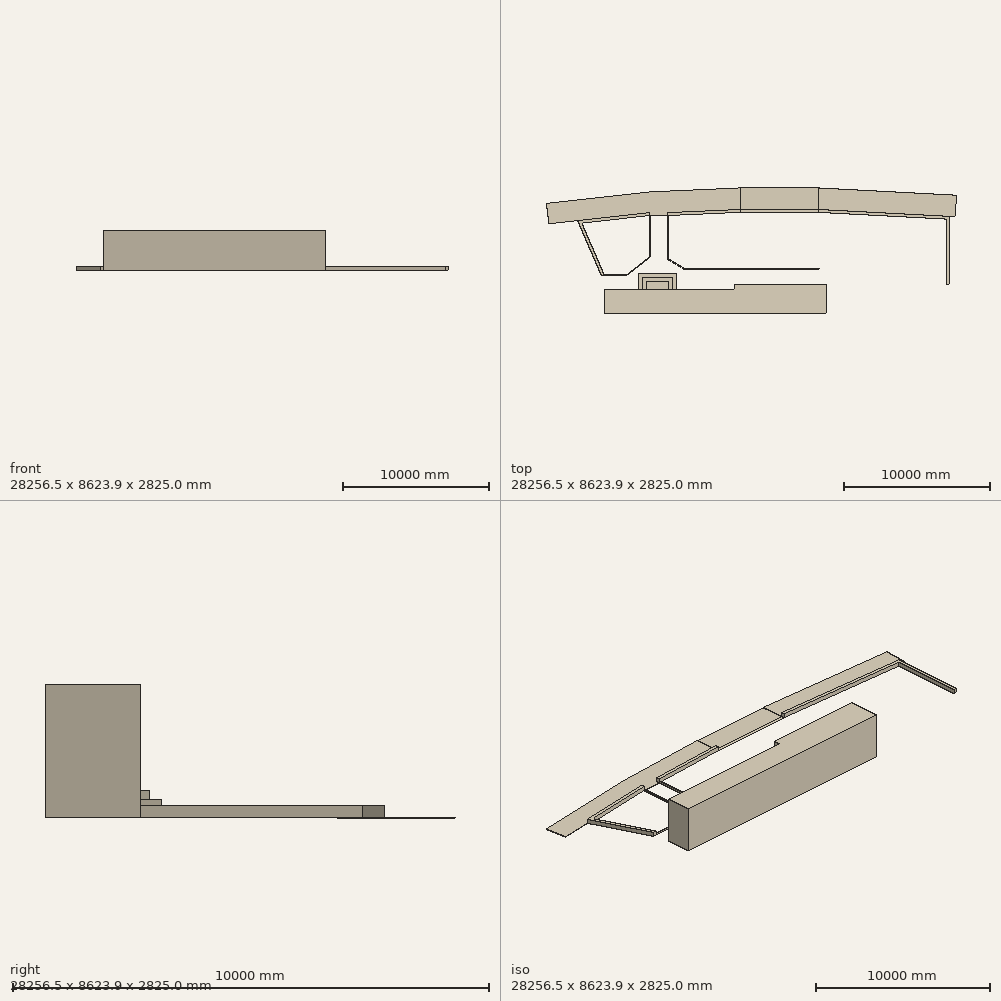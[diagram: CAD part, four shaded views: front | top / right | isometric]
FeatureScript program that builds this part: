
annotation { "Feature Type Name" : "Feature", "Feature Type Description" : "" }
export const myFeature = defineFeature(function(context is Context, id is Id, definition is map)
    precondition{}
    {
        {
            var Q0;
            Q0=qCreatedBy(makeId("Top.planeOp"),FACE);
            var sketch = newSketch(context, id + "F0", { "sketchPlane" : qUnion([Q0])});
            skLineSegment(sketch, "E0", {"start": v(0, 1000) * mm, "end": v(1590, 1000) * mm});
            skLineSegment(sketch, "E1", {"start": v(0, 1000) * mm, "end": v(-1557.02, 4597.51) * mm});
            skLineSegment(sketch, "E2", {"start": v(-1557.02, 4597.51) * mm, "end": v(3143.94, 5120.86) * mm});
            skLineSegment(sketch, "E3", {"start": v(3143.94, 5120.86) * mm, "end": v(3143.94, 2210.86) * mm});
            skLineSegment(sketch, "E4", {"start": v(3143.94, 2210.86) * mm, "end": v(1590, 1000) * mm});
            skLineSegment(sketch, "E5", {"start": v(4373.94, 5120.86) * mm, "end": v(9373.94, 5340) * mm});
            skLineSegment(sketch, "E6", {"start": v(9373.94, 5340) * mm, "end": v(14723.94, 5340) * mm, "construction": true});
            skLineSegment(sketch, "E7", {"start": v(14723.94, 5340) * mm, "end": v(23582.98, 4875.72) * mm});
            skLineSegment(sketch, "E8", {"start": v(23582.98, 4875.72) * mm, "end": v(23582.98, 400) * mm});
            skLineSegment(sketch, "E9", {"start": v(4373.94, 5120.86) * mm, "end": v(4373.94, 2100.86) * mm});
            skLineSegment(sketch, "E10", {"start": v(4373.94, 2100.86) * mm, "end": v(5527.75, 1400) * mm});
            skLineSegment(sketch, "E11", {"start": v(5527.75, 1400) * mm, "end": v(14847.75, 1400) * mm});
            skLineSegment(sketch, "E12", {"start": v(14847.75, 1400) * mm, "end": v(14847.75, 400) * mm});
            skLineSegment(sketch, "E13", {"start": v(0, 0) * mm, "end": v(8970, 0) * mm});
            skLineSegment(sketch, "E14", {"start": v(8970, 0) * mm, "end": v(8970, 400) * mm});
            skLineSegment(sketch, "E15", {"start": v(8970, 400) * mm, "end": v(14847.75, 400) * mm});
            skLineSegment(sketch, "E16", {"start": v(0, 0) * mm, "end": v(0, 1000) * mm, "construction": true});
            skLineSegment(sketch, "E17", {"start": v(3143.94, 5120.86) * mm, "end": v(4373.94, 5120.86) * mm, "construction": true});
            skLineSegment(sketch, "E18", {"start": v(2360, 0) * mm, "end": v(2360, 1120) * mm});
            skLineSegment(sketch, "E19", {"start": v(2360, 1120) * mm, "end": v(4990, 1120) * mm});
            skLineSegment(sketch, "E20", {"start": v(4990, 1120) * mm, "end": v(4990, 0) * mm});
            skLineSegment(sketch, "E21", {"start": v(2642.5, 0) * mm, "end": v(2642.5, 850) * mm});
            skLineSegment(sketch, "E22", {"start": v(2642.5, 850) * mm, "end": v(4707.5, 850) * mm});
            skLineSegment(sketch, "E23", {"start": v(4707.5, 850) * mm, "end": v(4707.5, 0) * mm});
            skLineSegment(sketch, "E24", {"start": v(2925, 0) * mm, "end": v(2925, 580) * mm});
            skLineSegment(sketch, "E25", {"start": v(2925, 580) * mm, "end": v(4425, 580) * mm});
            skLineSegment(sketch, "E26", {"start": v(4425, 580) * mm, "end": v(4425, 0) * mm});
            skLineSegment(sketch, "E27", {"start": v(2360, 1120) * mm, "end": v(2642.5, 850) * mm, "construction": true});
            skLineSegment(sketch, "E28", {"start": v(2642.5, 850) * mm, "end": v(2925, 580) * mm, "construction": true});
            skLineSegment(sketch, "E29", {"start": v(4425, 580) * mm, "end": v(4707.5, 850) * mm, "construction": true});
            skLineSegment(sketch, "E30", {"start": v(4707.5, 850) * mm, "end": v(4990, 1120) * mm, "construction": true});
            skLineSegment(sketch, "E31", {"start": v(2360, 1120) * mm, "end": v(2360, 1600) * mm, "construction": true});
            skLineSegment(sketch, "E32", {"start": v(-3990.98, 5956.54) * mm, "end": v(3143.94, 6750.86) * mm});
            skLineSegment(sketch, "E33", {"start": v(3143.94, 6750.86) * mm, "end": v(9373.94, 7023.9) * mm});
            skLineSegment(sketch, "E34", {"start": v(9373.94, 7023.9) * mm, "end": v(14723.94, 7023.9) * mm});
            skLineSegment(sketch, "E35", {"start": v(14723.94, 7023.9) * mm, "end": v(24265.47, 6523.86) * mm});
            skLineSegment(sketch, "E36", {"start": v(4373.94, 5120.86) * mm, "end": v(4373.94, 7645.58) * mm, "construction": true});
            skSolve(sketch);
        }
        {
            var Q0;
            {var subQ0=sQuery(id+"F0.wireOp",EDGE,"E24");Q0=makeQuery(id+"F0.imprint","IMPRINT",FACE,{"disambiguationData":[TD([[makeQuery(id+"F0.imprint","IMPRINT",EDGE,{"derivedFrom":subQ0}),-1.0]])]});}
            var sketch = newSketch(context, id + "F1", { "sketchPlane" : qUnion([Q0])});
            skLineSegment(sketch, "E37.bottom", {"start": v(4990, 1120) * mm, "end": v(2360, 1120) * mm});
            skLineSegment(sketch, "E37.top", {"start": v(4990, 0) * mm, "end": v(2360, 0) * mm});
            skLineSegment(sketch, "E37.left", {"start": v(4990, 1120) * mm, "end": v(4990, 0) * mm});
            skLineSegment(sketch, "E37.right", {"start": v(2360, 1120) * mm, "end": v(2360, 0) * mm});
            skSolve(sketch);
        }
        {
            var Q0;
            Q0 = qSketchRegion(id + "F1", true);
            extrude(context, id + "F2", {"entities" : qUnion([Q0]), "depth" : 190 * mm});
        }
        {
            var Q0;
            Q0=makeQuery(id+"F2.opExtrude","CAP_FACE",FACE,{"disambiguationData":[OSD([sQuery(id+"F1.wireOp",EDGE,"E37.bottom"),sQuery(id+"F1.wireOp",EDGE,"E37.top"),sQuery(id+"F1.wireOp",EDGE,"E37.left"),sQuery(id+"F1.wireOp",EDGE,"E37.right")])],"isStart":false});
            var sketch = newSketch(context, id + "F3", { "sketchPlane" : qUnion([Q0])});
            skLineSegment(sketch, "E38.bottom", {"start": v(4707.5, 850) * mm, "end": v(2642.5, 850) * mm});
            skLineSegment(sketch, "E38.top", {"start": v(4707.5, 0) * mm, "end": v(2642.5, 0) * mm});
            skLineSegment(sketch, "E38.left", {"start": v(4707.5, 850) * mm, "end": v(4707.5, 0) * mm});
            skLineSegment(sketch, "E38.right", {"start": v(2642.5, 850) * mm, "end": v(2642.5, 0) * mm});
            skSolve(sketch);
        }
        {
            var Q0;
            Q0 = qSketchRegion(id + "F3", true);
            extrude(context, id + "F4", {"entities" : qUnion([Q0]), "operationType" : NewBodyOperationType.ADD, "depth" : 190 * mm});
        }
        {
            var Q0;
            Q0=makeQuery(id+"F4.opExtrude","CAP_FACE",FACE,{"disambiguationData":[OSD([sQuery(id+"F3.wireOp",EDGE,"E38.bottom"),sQuery(id+"F3.wireOp",EDGE,"E38.top"),sQuery(id+"F3.wireOp",EDGE,"E38.left"),sQuery(id+"F3.wireOp",EDGE,"E38.right")])],"isStart":false});
            var sketch = newSketch(context, id + "F5", { "sketchPlane" : qUnion([Q0])});
            skLineSegment(sketch, "E39.bottom", {"start": v(4425, 580) * mm, "end": v(2925, 580) * mm});
            skLineSegment(sketch, "E39.top", {"start": v(4425, 0) * mm, "end": v(2925, 0) * mm});
            skLineSegment(sketch, "E39.left", {"start": v(4425, 580) * mm, "end": v(4425, 0) * mm});
            skLineSegment(sketch, "E39.right", {"start": v(2925, 580) * mm, "end": v(2925, 0) * mm});
            skSolve(sketch);
        }
        {
            var Q0;
            Q0 = qSketchRegion(id + "F5", true);
            extrude(context, id + "F6", {"entities" : qUnion([Q0]), "operationType" : NewBodyOperationType.ADD, "depth" : 190 * mm});
        }
        {
            var Q0;
            Q0=makeQuery(id+"F0.imprint","IMPRINT",FACE,{"disambiguationData":[TD([[makeQuery(id+"F0.imprint","IMPRINT",EDGE,{"derivedFrom":sQuery(id+"F0.wireOp",EDGE,"E0")}),1.0]])]});
            var sketch = newSketch(context, id + "F7", { "sketchPlane" : qUnion([Q0])});
            skLineSegment(sketch, "E40", {"start": v(0, 1000) * mm, "end": v(-1557.02, 4597.51) * mm});
            skLineSegment(sketch, "E41", {"start": v(-1557.02, 4597.51) * mm, "end": v(3143.94, 5120.86) * mm});
            skLineSegment(sketch, "E42", {"start": v(3143.94, 5120.86) * mm, "end": v(3121.8, 5319.63) * mm});
            skLineSegment(sketch, "E43", {"start": v(3121.8, 5319.63) * mm, "end": v(-1848.02, 4766.35) * mm});
            skLineSegment(sketch, "E44", {"start": v(-1848.02, 4766.35) * mm, "end": v(-217.93, 1000) * mm});
            skLineSegment(sketch, "E45", {"start": v(-217.93, 1000) * mm, "end": v(0, 1000) * mm});
            skLineSegment(sketch, "E46", {"start": v(-1557.02, 4597.51) * mm, "end": v(-1740.57, 4518.07) * mm, "construction": true});
            skLineSegment(sketch, "E47", {"start": v(4373.94, 5120.86) * mm, "end": v(4351.8, 5319.63) * mm});
            skLineSegment(sketch, "E48", {"start": v(4351.8, 5319.63) * mm, "end": v(9373.94, 5539.74) * mm});
            skLineSegment(sketch, "E49", {"start": v(9373.94, 5539.74) * mm, "end": v(9373.94, 5340) * mm});
            skLineSegment(sketch, "E50", {"start": v(9373.94, 5340) * mm, "end": v(4373.94, 5120.86) * mm});
            skLineSegment(sketch, "E51", {"start": v(14723.94, 5340) * mm, "end": v(14723.94, 5539.74) * mm});
            skLineSegment(sketch, "E52", {"start": v(14723.94, 5539.74) * mm, "end": v(23782.72, 5065) * mm});
            skLineSegment(sketch, "E53", {"start": v(23782.72, 5065) * mm, "end": v(23782.72, 400) * mm});
            skLineSegment(sketch, "E54", {"start": v(23782.72, 400) * mm, "end": v(23582.98, 400) * mm});
            skLineSegment(sketch, "E55", {"start": v(23582.98, 400) * mm, "end": v(23582.98, 4875.72) * mm});
            skLineSegment(sketch, "E56", {"start": v(23582.98, 4875.72) * mm, "end": v(14723.94, 5340) * mm});
            skSolve(sketch);
        }
        {
            var Q0;
            Q0 = qSketchRegion(id + "F7", true);
            extrude(context, id + "F8", {"entities" : qUnion([Q0]), "depth" : 260 * mm});
        }
        {
            var Q0;
            Q0=makeQuery(id+"F0.imprint","IMPRINT",FACE,{"disambiguationData":[TD([[makeQuery(id+"F0.imprint","IMPRINT",EDGE,{"derivedFrom":sQuery(id+"F0.wireOp",EDGE,"E0")}),1.0]])]});
            var sketch = newSketch(context, id + "F9", { "sketchPlane" : qUnion([Q0])});
            skLineSegment(sketch, "E57", {"start": v(4373.94, 5120.86) * mm, "end": v(4373.94, 2100.86) * mm});
            skLineSegment(sketch, "E58", {"start": v(4373.94, 2100.86) * mm, "end": v(5527.75, 1400) * mm});
            skLineSegment(sketch, "E59", {"start": v(5527.75, 1400) * mm, "end": v(14847.75, 1400) * mm});
            skLineSegment(sketch, "E60", {"start": v(14847.75, 1400) * mm, "end": v(14847.75, 1450) * mm});
            skLineSegment(sketch, "E61", {"start": v(14847.75, 1450) * mm, "end": v(5541.75, 1450) * mm});
            skLineSegment(sketch, "E62", {"start": v(5541.75, 1450) * mm, "end": v(4423.94, 2128.99) * mm});
            skLineSegment(sketch, "E63", {"start": v(4423.94, 2128.99) * mm, "end": v(4423.94, 5123.05) * mm});
            skLineSegment(sketch, "E64", {"start": v(4423.94, 5123.05) * mm, "end": v(4373.94, 5120.86) * mm});
            skLineSegment(sketch, "E65", {"start": v(3143.94, 5120.86) * mm, "end": v(3143.94, 2210.86) * mm});
            skLineSegment(sketch, "E66", {"start": v(3143.94, 2210.86) * mm, "end": v(1590, 1000) * mm});
            skLineSegment(sketch, "E67", {"start": v(1590, 1000) * mm, "end": v(0, 1000) * mm});
            skLineSegment(sketch, "E68", {"start": v(0, 1000) * mm, "end": v(-21.64, 1050) * mm});
            skLineSegment(sketch, "E69", {"start": v(-21.64, 1050) * mm, "end": v(1572.82, 1050) * mm});
            skLineSegment(sketch, "E70", {"start": v(1572.82, 1050) * mm, "end": v(3093.94, 2235.29) * mm});
            skLineSegment(sketch, "E71", {"start": v(3093.94, 2235.29) * mm, "end": v(3093.94, 5115.3) * mm});
            skLineSegment(sketch, "E72", {"start": v(3093.94, 5115.3) * mm, "end": v(3143.94, 5120.86) * mm});
            skLineSegment(sketch, "E73", {"start": v(3093.94, 2235.29) * mm, "end": v(3143.94, 2235.29) * mm, "construction": true});
            skLineSegment(sketch, "E74", {"start": v(1572.82, 1050) * mm, "end": v(1572.82, 1000) * mm, "construction": true});
            skLineSegment(sketch, "E75", {"start": v(3143.94, 2210.86) * mm, "end": v(3113.2, 2250.3) * mm, "construction": true});
            skLineSegment(sketch, "E76", {"start": v(5541.75, 1450) * mm, "end": v(5515.8, 1407.27) * mm, "construction": true});
            skLineSegment(sketch, "E77", {"start": v(4423.94, 2128.99) * mm, "end": v(4373.94, 2128.99) * mm, "construction": true});
            skSolve(sketch);
        }
        {
            var Q0;
            Q0 = qSketchRegion(id + "F9", true);
            extrude(context, id + "F10", {"entities" : qUnion([Q0]), "depth" : 110 * mm});
        }
        {
            var Q0;
            Q0=makeQuery(id+"F0.imprint","IMPRINT",FACE,{"disambiguationData":[TD([[makeQuery(id+"F0.imprint","IMPRINT",EDGE,{"derivedFrom":sQuery(id+"F0.wireOp",EDGE,"E0")}),1.0]])]});
            var sketch = newSketch(context, id + "F11", { "sketchPlane" : qUnion([Q0])});
            skLineSegment(sketch, "E78", {"start": v(15277.75, 400) * mm, "end": v(8970, 400) * mm});
            skLineSegment(sketch, "E79", {"start": v(8970, 400) * mm, "end": v(8970, 0) * mm});
            skLineSegment(sketch, "E80", {"start": v(8970, 0) * mm, "end": v(0, 0) * mm});
            skLineSegment(sketch, "E81", {"start": v(0, 0) * mm, "end": v(0, -1600) * mm});
            skLineSegment(sketch, "E82", {"start": v(0, -1600) * mm, "end": v(15277.75, -1600) * mm});
            skLineSegment(sketch, "E83", {"start": v(15277.75, -1600) * mm, "end": v(15277.75, 400) * mm});
            skSolve(sketch);
        }
        {
            var Q0;
            Q0 = qSketchRegion(id + "F11", true);
            extrude(context, id + "F12", {"entities" : qUnion([Q0]), "depth" : 2800 * mm});
        }
        {
            var Q0;
            Q0=makeQuery(id+"F12.opExtrude","SWEPT_FACE",FACE,{"disambiguationData":[OSD([sQuery(id+"F11.wireOp",EDGE,"E80")])]});
            var sketch = newSketch(context, id + "F13", { "sketchPlane" : qUnion([Q0])});
            skLineSegment(sketch, "E84.bottom", {"start": v(-4175, 570) * mm, "end": v(-3175, 570) * mm});
            skLineSegment(sketch, "E84.top", {"start": v(-4175, 2570) * mm, "end": v(-3175, 2570) * mm});
            skLineSegment(sketch, "E84.left", {"start": v(-4175, 570) * mm, "end": v(-4175, 2570) * mm});
            skLineSegment(sketch, "E84.right", {"start": v(-3175, 570) * mm, "end": v(-3175, 2570) * mm});
            skLineSegment(sketch, "E85", {"start": v(-3675, 2570) * mm, "end": v(-3675, 570) * mm, "construction": true});
            skSolve(sketch);
        }
        {
            var Q0;
            Q0 = qSketchRegion(id + "F13", true);
            extrude(context, id + "F14", {"entities" : qUnion([Q0]), "operationType" : NewBodyOperationType.REMOVE, "oppositeDirection" : true, "depth" : 100 * mm});
        }
        {
            var Q0;
            Q0=qCreatedBy(makeId("Top.planeOp"),FACE);
            var sketch = newSketch(context, id + "F15", { "sketchPlane" : qUnion([Q0])});
            skLineSegment(sketch, "E86", {"start": v(-3990.98, 5956.54) * mm, "end": v(3143.94, 6750.86) * mm});
            skLineSegment(sketch, "E87", {"start": v(3143.94, 6750.86) * mm, "end": v(9373.94, 7023.9) * mm});
            skLineSegment(sketch, "E88", {"start": v(9373.94, 7023.9) * mm, "end": v(14723.94, 7023.9) * mm});
            skLineSegment(sketch, "E89", {"start": v(14723.94, 7023.9) * mm, "end": v(24265.47, 6523.86) * mm});
            skLineSegment(sketch, "E90", {"start": v(24265.47, 6523.86) * mm, "end": v(24187.9, 5043.76) * mm});
            skLineSegment(sketch, "E91", {"start": v(24187.9, 5043.76) * mm, "end": v(14723.94, 5539.74) * mm});
            skLineSegment(sketch, "E92", {"start": v(9373.94, 5539.74) * mm, "end": v(4351.8, 5319.63) * mm});
            skLineSegment(sketch, "E93", {"start": v(4351.8, 5319.63) * mm, "end": v(4373.94, 5120.86) * mm});
            skLineSegment(sketch, "E94", {"start": v(4373.94, 5120.86) * mm, "end": v(3143.94, 5120.86) * mm});
            skLineSegment(sketch, "E95", {"start": v(3143.94, 5120.86) * mm, "end": v(3121.8, 5319.63) * mm});
            skLineSegment(sketch, "E96", {"start": v(3121.8, 5319.63) * mm, "end": v(-3833.86, 4545.27) * mm});
            skLineSegment(sketch, "E97", {"start": v(-3833.86, 4545.27) * mm, "end": v(-3990.98, 5956.54) * mm});
            skLineSegment(sketch, "E98", {"start": v(9373.94, 5539.74) * mm, "end": v(9373.94, 5340) * mm});
            skLineSegment(sketch, "E99", {"start": v(9373.94, 5340) * mm, "end": v(14723.94, 5340) * mm});
            skLineSegment(sketch, "E100", {"start": v(14723.94, 5340) * mm, "end": v(14723.94, 5539.74) * mm});
            skSolve(sketch);
        }
        {
            var Q0;
            Q0 = qSketchRegion(id + "F15", true);
            extrude(context, id + "F16", {"entities" : qUnion([Q0]), "oppositeDirection" : true, "depth" : 25 * mm});
        }
        {
            var Q0;
            Q0=qCreatedBy(makeId("Right.planeOp"),FACE);
            var Q1;
            Q1=makeQuery(id+"F8.opExtrude","CAP_VERTEX",VERTEX,{"disambiguationData":[OSD([sQuery(id+"F7.wireOp",EDGE,"E48"),sQuery(id+"F7.wireOp",EDGE,"E49")])],"isStart":true});
            cPlane(context, id + "F17", {"entities" : qUnion([Q0, Q1]), "cplaneType" : CPlaneType.PLANE_POINT, "offset" : 25 * mm, "width" : 150 * mm, "height" : 150 * mm});
        }
        {
            var Q0;
            Q0=qCreatedBy(id+"F17.planeOp",FACE);
            var sketch = newSketch(context, id + "F18", { "sketchPlane" : qUnion([Q0])});
            skLineSegment(sketch, "E101", {"start": v(5539.74, 0) * mm, "end": v(7023.9, -25) * mm});
            skLineSegment(sketch, "E102", {"start": v(7023.9, -25) * mm, "end": v(7023.9, 0) * mm});
            skLineSegment(sketch, "E103", {"start": v(7023.9, 0) * mm, "end": v(5539.74, 0) * mm});
            skSolve(sketch);
        }
        {
            var Q0;
            Q0 = qSketchRegion(id + "F18", true);
            var Q1;
            Q1=makeQuery(id+"F8.opExtrude","SWEPT_FACE",FACE,{"disambiguationData":[OSD([sQuery(id+"F7.wireOp",EDGE,"E51")])]});
            extrude(context, id + "F19", {"entities" : qUnion([Q0]), "operationType" : NewBodyOperationType.REMOVE, "endBound" : BoundingType.UP_TO_SURFACE, "endBoundEntityFace" : qUnion([Q1]), "depth" : 25 * mm});
        }
    });
